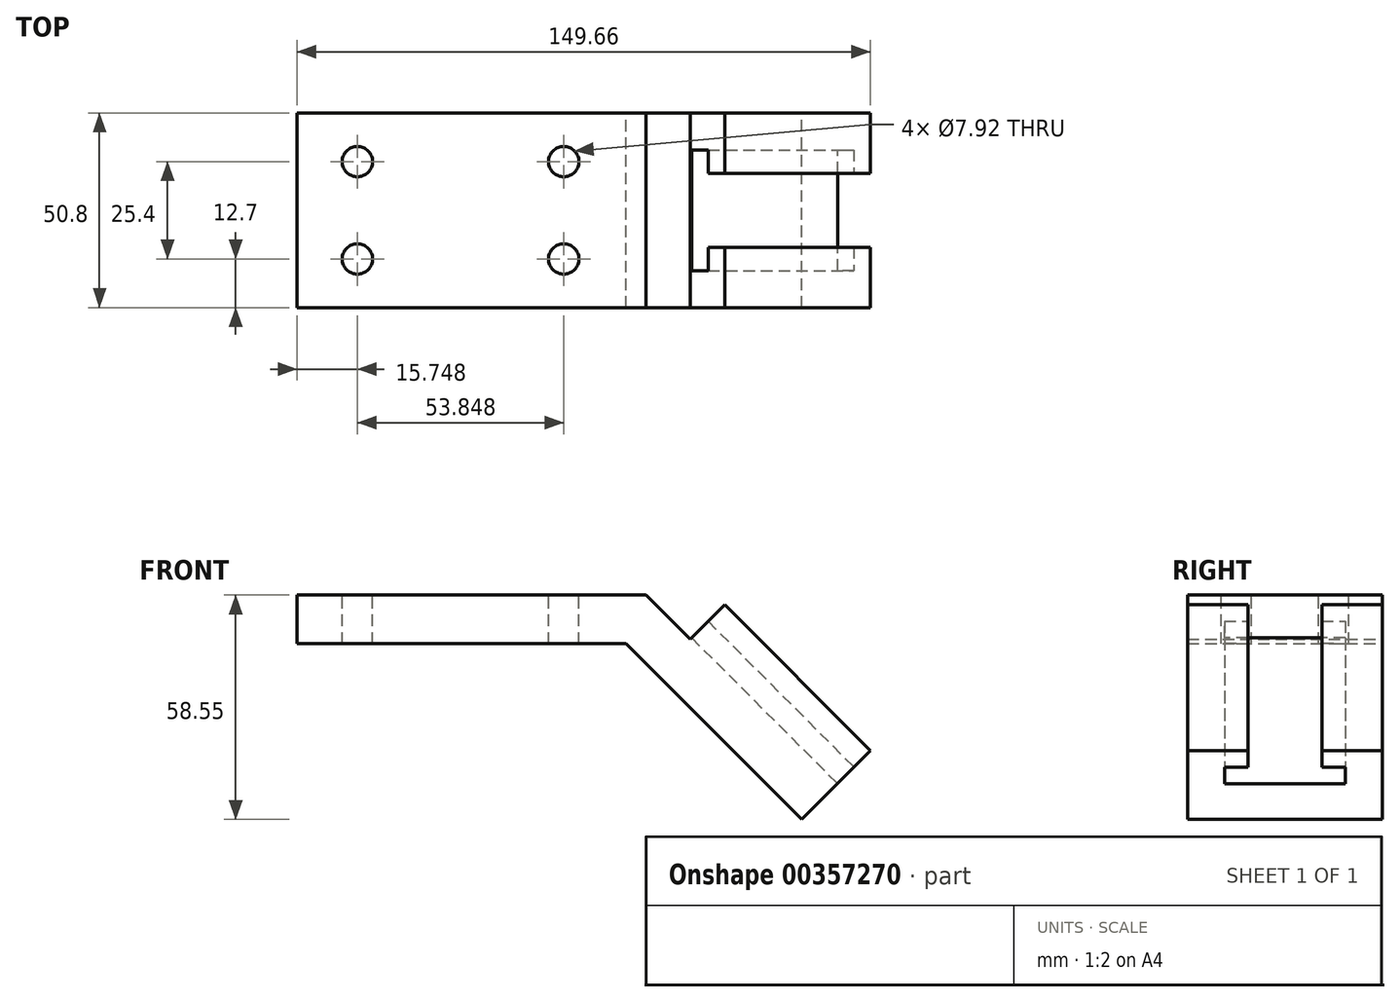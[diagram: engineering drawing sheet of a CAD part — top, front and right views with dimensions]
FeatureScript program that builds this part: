
annotation { "Feature Type Name" : "Feature", "Feature Type Description" : "" }
export const myFeature = defineFeature(function(context is Context, id is Id, definition is map)
    precondition{}
    {
        {
            var Q0;
            Q0=qCreatedBy(makeId("Front.planeOp"),FACE);
            var sketch = newSketch(context, id + "F0", { "sketchPlane" : qUnion([Q0])});
            skLineSegment(sketch, "E0", {"start": v(0, 0) * mm, "end": v(0, 12.7) * mm});
            skLineSegment(sketch, "E1", {"start": v(0, 12.7) * mm, "end": v(91.11, 12.7) * mm});
            skLineSegment(sketch, "E2", {"start": v(131.7, -45.85) * mm, "end": v(85.85, 0) * mm});
            skLineSegment(sketch, "E3", {"start": v(85.85, 0) * mm, "end": v(0, 0) * mm});
            skLineSegment(sketch, "E4", {"start": v(91.11, 12.7) * mm, "end": v(102.6, 1.2) * mm});
            skLineSegment(sketch, "E5", {"start": v(102.6, 1.2) * mm, "end": v(111.59, 10.19) * mm});
            skLineSegment(sketch, "E6", {"start": v(111.59, 10.19) * mm, "end": v(149.66, -27.9) * mm});
            skLineSegment(sketch, "E7", {"start": v(149.66, -27.9) * mm, "end": v(131.7, -45.85) * mm});
            skLineSegment(sketch, "E8", {"start": v(102.6, 1.2) * mm, "end": v(140.68, -36.87) * mm, "construction": true});
            skSolve(sketch);
        }
        {
            var Q0;
            Q0=makeQuery(id+"F0.imprint","IMPRINT",FACE,{"disambiguationData":[TD([[makeQuery(id+"F0.imprint","IMPRINT",EDGE,{"derivedFrom":sQuery(id+"F0.wireOp",EDGE,"E0")}),-1.0]])]});
            extrude(context, id + "F1", {"entities" : qUnion([Q0]), "endBound" : BoundingType.SYMMETRIC, "depth" : 50.8 * mm});
        }
        {
            var Q0;
            Q0=makeQuery(id+"F1.opExtrude","SWEPT_FACE",FACE,{"disambiguationData":[OSD([sQuery(id+"F0.wireOp",EDGE,"E7")])]});
            var sketch = newSketch(context, id + "F2", { "sketchPlane" : qUnion([Q0])});
            skLineSegment(sketch, "E9", {"start": v(-25.4, 86.1) * mm, "end": v(-9.65, 86.1) * mm});
            skLineSegment(sketch, "E10", {"start": v(-9.65, 86.1) * mm, "end": v(-9.65, 80.01) * mm});
            skLineSegment(sketch, "E11", {"start": v(-9.65, 80.01) * mm, "end": v(-15.75, 80.01) * mm});
            skLineSegment(sketch, "E12", {"start": v(-15.75, 80.01) * mm, "end": v(-15.75, 73.91) * mm});
            skLineSegment(sketch, "E13", {"start": v(-15.75, 73.91) * mm, "end": v(15.75, 73.91) * mm});
            skLineSegment(sketch, "E14", {"start": v(15.75, 73.91) * mm, "end": v(15.75, 80.01) * mm});
            skLineSegment(sketch, "E15", {"start": v(15.75, 80.01) * mm, "end": v(9.65, 80.01) * mm});
            skLineSegment(sketch, "E16", {"start": v(9.65, 80.01) * mm, "end": v(9.65, 86.1) * mm});
            skLineSegment(sketch, "E17", {"start": v(9.65, 86.1) * mm, "end": v(25.4, 86.1) * mm});
            skLineSegment(sketch, "E18", {"start": v(-9.65, 86.1) * mm, "end": v(9.65, 86.1) * mm});
            skSolve(sketch);
        }
        {
            var Q0;
            Q0 = qSketchRegion(id + "F2", true);
            extrude(context, id + "F3", {"entities" : qUnion([Q0]), "operationType" : NewBodyOperationType.REMOVE, "endBound" : BoundingType.THROUGH_ALL, "oppositeDirection" : true, "depth" : 25.4 * mm});
        }
        {
            var Q0;
            Q0=makeQuery(id+"F1.opExtrude","SWEPT_FACE",FACE,{"disambiguationData":[OSD([sQuery(id+"F0.wireOp",EDGE,"E2")])]});
            var sketch = newSketch(context, id + "F4", { "sketchPlane" : qUnion([Q0])});
            skArc(sketch, "E19", {"start": v(119.18, -25.4) * mm, "mid": v(125.55, 0) * mm, "end": v(119.18, 25.4) * mm});
            skLineSegment(sketch, "E20", {"start": v(119.18, -25.4) * mm, "end": v(125.55, -25.4) * mm});
            skLineSegment(sketch, "E21", {"start": v(119.18, 25.4) * mm, "end": v(125.55, 25.4) * mm});
            skLineSegment(sketch, "E22", {"start": v(125.55, 25.4) * mm, "end": v(125.55, 0) * mm});
            skLineSegment(sketch, "E23", {"start": v(125.55, 0) * mm, "end": v(125.55, -25.4) * mm});
            skSolve(sketch);
        }
        {
            var Q0;
            Q0 = qSketchRegion(id + "F4", true);
            extrude(context, id + "F5", {"entities" : qUnion([Q0]), "operationType" : NewBodyOperationType.REMOVE, "oppositeDirection" : true, "depth" : 25.4 * mm});
        }
        {
            var Q0;
            Q0=makeQuery(id+"F1.opExtrude","SWEPT_FACE",FACE,{"disambiguationData":[OSD([sQuery(id+"F0.wireOp",EDGE,"E1")])]});
            var sketch = newSketch(context, id + "F6", { "sketchPlane" : qUnion([Q0])});
            skCircle(sketch, "E24", {"center": v(15.75, 12.7) * mm, "radius": 3.96 * mm});
            skCircle(sketch, "E25", {"center": v(69.6, 12.7) * mm, "radius": 3.96 * mm});
            skCircle(sketch, "E26", {"center": v(15.75, -12.7) * mm, "radius": 3.96 * mm});
            skCircle(sketch, "E27", {"center": v(69.6, -12.7) * mm, "radius": 3.96 * mm});
            skSolve(sketch);
        }
        {
            var Q0;
            Q0=makeQuery(id+"F6.imprint","IMPRINT",FACE,{"disambiguationData":[TD([[makeQuery(id+"F6.imprint","IMPRINT",EDGE,{"derivedFrom":sQuery(id+"F6.wireOp",EDGE,"E25")}),1.0]])]});
            var Q1;
            Q1=makeQuery(id+"F6.imprint","IMPRINT",FACE,{"disambiguationData":[TD([[makeQuery(id+"F6.imprint","IMPRINT",EDGE,{"derivedFrom":sQuery(id+"F6.wireOp",EDGE,"E24")}),1.0]])]});
            var Q2;
            Q2=makeQuery(id+"F6.imprint","IMPRINT",FACE,{"disambiguationData":[TD([[makeQuery(id+"F6.imprint","IMPRINT",EDGE,{"derivedFrom":sQuery(id+"F6.wireOp",EDGE,"E26")}),1.0]])]});
            var Q3;
            Q3=makeQuery(id+"F6.imprint","IMPRINT",FACE,{"disambiguationData":[TD([[makeQuery(id+"F6.imprint","IMPRINT",EDGE,{"derivedFrom":sQuery(id+"F6.wireOp",EDGE,"E27")}),1.0]])]});
            extrude(context, id + "F7", {"entities" : qUnion([Q0, Q1, Q2, Q3]), "operationType" : NewBodyOperationType.REMOVE, "oppositeDirection" : true, "depth" : 25.4 * mm});
        }
    });
